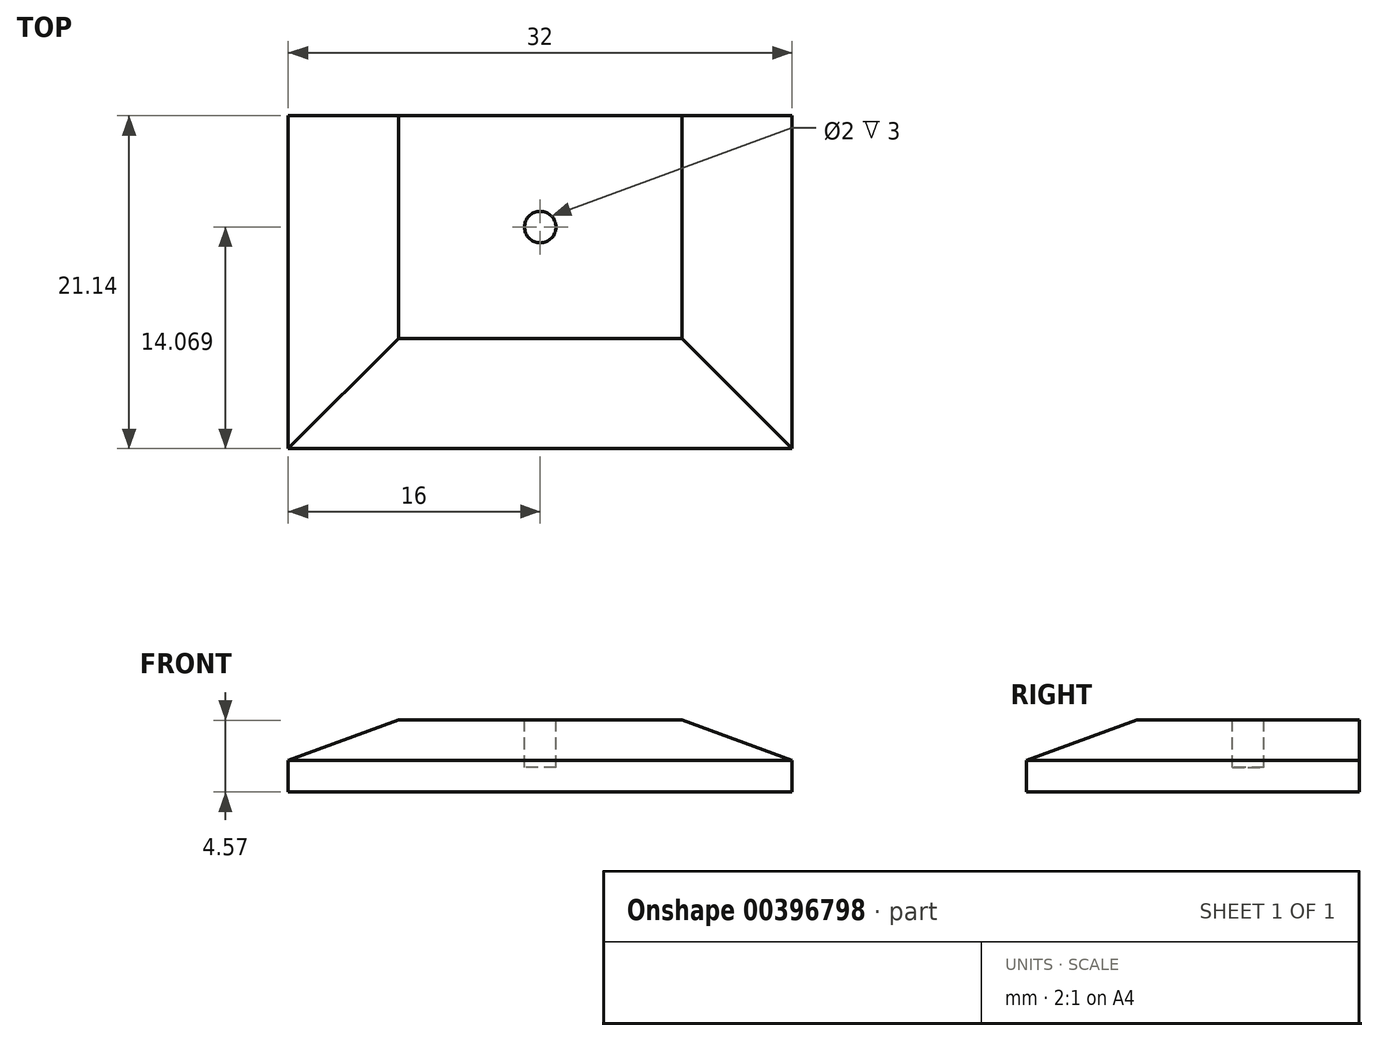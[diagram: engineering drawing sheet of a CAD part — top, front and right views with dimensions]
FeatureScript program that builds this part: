
annotation { "Feature Type Name" : "Feature", "Feature Type Description" : "" }
export const myFeature = defineFeature(function(context is Context, id is Id, definition is map)
    precondition{}
    {
        {
            assignVariable(context, id + "F0", {"name" : "SizeDivision", "anyValue" : 17.5});
        }
        {
            var Q0;
            Q0=qCreatedBy(makeId("Top.planeOp"),FACE);
            var sketch = newSketch(context, id + "F1", { "sketchPlane" : qUnion([Q0])});
            skLineSegment(sketch, "E0.bottom", {"start": v(0, 0) * mm, "end": v(32, 0) * mm});
            skLineSegment(sketch, "E0.top", {"start": v(0, -21.14) * mm, "end": v(32, -21.14) * mm});
            skLineSegment(sketch, "E0.left", {"start": v(0, 0) * mm, "end": v(0, -21.14) * mm});
            skLineSegment(sketch, "E0.right", {"start": v(32, 0) * mm, "end": v(32, -21.14) * mm});
            skSolve(sketch);
        }
        {
            var Q0;
            Q0 = qSketchRegion(id + "F1", true);
            extrude(context, id + "F2", {"entities" : qUnion([Q0]), "depth" : (80 / getVariable(context, 'SizeDivision')) * mm});
        }
        {
            var Q0;
            Q0=makeQuery(id+"F2.opExtrude","CAP_EDGE",EDGE,{"disambiguationData":[OSD([sQuery(id+"F1.wireOp",EDGE,"E0.left")])],"isStart":false});
            var Q1;
            Q1=makeQuery(id+"F2.opExtrude","CAP_EDGE",EDGE,{"disambiguationData":[OSD([sQuery(id+"F1.wireOp",EDGE,"E0.top")])],"isStart":false});
            var Q2;
            Q2=makeQuery(id+"F2.opExtrude","CAP_EDGE",EDGE,{"disambiguationData":[OSD([sQuery(id+"F1.wireOp",EDGE,"E0.right")])],"isStart":false});
            chamfer(context, id + "F3", {"entities" : qUnion([Q0, Q1, Q2]), "chamferType" : ChamferType.OFFSET_ANGLE, "width" : 7 * mm, "oppositeDirection" : false, "angle" : 20 * degree, "tangentPropagation" : true});
        }
        {
            var Q0;
            Q0=makeQuery(id+"F2.opExtrude","CAP_FACE",FACE,{"disambiguationData":[OSD([sQuery(id+"F1.wireOp",EDGE,"E0.bottom"),sQuery(id+"F1.wireOp",EDGE,"E0.top"),sQuery(id+"F1.wireOp",EDGE,"E0.left"),sQuery(id+"F1.wireOp",EDGE,"E0.right")])],"isStart":false});
            var sketch = newSketch(context, id + "F4", { "sketchPlane" : qUnion([Q0])});
            skLineSegment(sketch, "E1", {"start": v(16, -14.14) * mm, "end": v(16, 0) * mm, "construction": true});
            skCircle(sketch, "E2", {"center": v(16, -7.07) * mm, "radius": 1 * mm});
            skSolve(sketch);
        }
        {
            var Q0;
            Q0 = qSketchRegion(id + "F4", true);
            extrude(context, id + "F5", {"entities" : qUnion([Q0]), "operationType" : NewBodyOperationType.REMOVE, "oppositeDirection" : true, "depth" : 3 * mm});
        }
    });
